# Revit family: Hager-VOLTA-Flush_mounted-IP30-With_Cover-With_DIN-Hosted-PL-en
name_source: partatom
category: Electrical Equipment
units: mm (PartAtom-declared; Revit-internal decimal feet)

## family parameters
Cut with Voids When Loaded = No
Host = Face
Maintain Annotation Orientation = Yes
Panel Configuration = Two Columns, Circuits Across
Part Type = Panelboard
Room Calculation Point = No
Round Connector Dimension = Use Diameter
Shared = No

## types (18) — shared parameters
BC_MODEL_ID = 1547210
BC_OBJECT_ID = 513496
BC_OBJECT_VERSION = #5
Code hager = ADD-EC000214_EU
EF000003 - Mounting method = Flush-mounted
EF000007 - Colour = White
EF000008 - Width = 348 mm  [stored 1.14173 ft]
EF000024 - UV resistant = No
EF000049 - Depth = 98 mm  [stored 0.321522 ft]
EF000116 - RAL-number = 9010
EF001062 - EMC-version = No
EF001088 - Extension possible = Yes
EF001134 - DIN-rail = Yes
EF002950 - Width in number of modular spacings = 12
EF004462 - Type of closure = Other
EF005474 - Degree of protection (IP) = IP30
EF006244 - Transparent cover/door = No
EF006306 - With lock = No
EF009212 - Cover model = With notch
EF015941 - Signal passing door = No
ETIM class code = EC000214
ETIM class name = Small distribution board
HG000002-With door or cover = Yes
HG000003-Range = VOLTA
HG000005-Thickness = 2 mm  [stored 0.00656168 ft]
HG000006-Flush mounted = Yes
HG000009-Double swing door = No
HG000010-Asymmetric doors = No
HG000012-Door swing angle = 90.00°
HG000013-Door on the left = No
HG000014-Door on the right = Yes
HG000015-Clearance visibility = Yes
HG000016-Door 3D visibility = Yes
HG000017-Distance between poles = 18 mm  [stored 0.0590551 ft]
HG000060-RAL-number = 9010
HG000099-Onfly Template ID = 507532
HGEF002950-Width in number of modular spacings = 12
Manufacturer = Hager
Name = VOLTA-Flush_mounted-IP30-With_Cover-With_DIN-PL
Name BIM&CO = Electricity
Name hager = ADD_Enclosures_EC000214
Uniformat = Low Tension Service & Dist.
Uniformat code = D501001
zero-valued in all types: Default Elevation, EF001131 - Inner depth, HG000007-Number of empty columns

## per-type parameters (varying)
| type | BC_VARIANT_ID | EF000040 - Height | EF000118 - With mounting plate | EF000218 - Built-in depth | EF000266 - Number of rows | EF000332 - Built-in height | EF000846 - Built-in width | EF015776 - Earthing terminal block | EF015777 - Neutral terminal block | HG000001-Number of columns | HG000004-Manufacturer reference | HG000008-Number of empty rows | HG000011-Empty rows from bottom | HGEF000266-Number of rows |
| VOLTA-Flush_mounted_W348_H356_D98_12_Modular_Spacing-VU12AT | 1174376 | 356 mm  [stored 1.16798 ft] | No | 89 mm  [stored 0.291995 ft] | 1 | 321 mm  [stored 1.05315 ft] | 315 mm | Yes | Yes | 1 | VU12AT | 0 | No | 1 |
| VOLTA-Flush_mounted_W348_H356_D98_12_Modular_Spacing-VU12NE | 1174377 | 356 mm  [stored 1.16798 ft] | No | 89 mm  [stored 0.291995 ft] | 1 | 321 mm  [stored 1.05315 ft] | 315 mm | Yes | No | 1 | VU12NE | 0 | No | 1 |
| VOLTA-Flush_mounted_W348_H505_D98_12_Modular_Spacing-VU24AT | 1174378 | 505 mm  [stored 1.65682 ft] | No | 89 mm  [stored 0.291995 ft] | 2 | 470 mm  [stored 1.54199 ft] | 315 mm | Yes | Yes | 1 | VU24AT | 0 | No | 2 |
| VOLTA-Flush_mounted_W348_H505_D98_12_Modular_Spacing-VU24NE | 1174380 | 505 mm  [stored 1.65682 ft] | No | 89 mm  [stored 0.291995 ft] | 2 | 470 mm  [stored 1.54199 ft] | 315 mm | Yes | No | 1 | VU24NE | 0 | No | 2 |
| VOLTA-Flush_mounted_W348_H505_D98_12_Modular_Spacing-VU24NWB | 1174383 | 505 mm  [stored 1.65682 ft] | Yes | 89 mm  [stored 0.291995 ft] | 0 | 470 mm  [stored 1.54199 ft] | 315 mm | No | No | 0 | VU24NWB | 0 | No | 0 |
| VOLTA-Flush_mounted_W348_H630_D98_12_Modular_Spacing-VU36AT | 1174385 | 630 mm  [stored 2.06693 ft] | No | 89 mm  [stored 0.291995 ft] | 3 | 595 mm  [stored 1.9521 ft] | 315 mm | Yes | Yes | 1 | VU36AT | 0 | No | 3 |
| VOLTA-Flush_mounted_W348_H630_D98_12_Modular_Spacing-VU36NE | 1174386 | 630 mm  [stored 2.06693 ft] | No | 89 mm  [stored 0.291995 ft] | 3 | 595 mm  [stored 1.9521 ft] | 315 mm | Yes | No | 1 | VU36NE | 0 | No | 3 |
| VOLTA-Flush_mounted_W348_H630_D98_12_Modular_Spacing-VU36NWB | 1174387 | 630 mm  [stored 2.06693 ft] | Yes | 89 mm  [stored 0.291995 ft] | 0 | 595 mm  [stored 1.9521 ft] | 315 mm | No | No | 0 | VU36NWB | 0 | No | 0 |
| VOLTA-Flush_mounted_W348_H755_D98_12_Modular_Spacing-VU48AT | 1174388 | 755 mm  [stored 2.47703 ft] | No | 89 mm  [stored 0.291995 ft] | 4 | 720 mm  [stored 2.3622 ft] | 315 mm | Yes | Yes | 1 | VU48AT | 0 | No | 4 |
| VOLTA-Flush_mounted_W348_H755_D98_12_Modular_Spacing-VU48NE | 1174389 | 755 mm  [stored 2.47703 ft] | No | 89 mm  [stored 0.291995 ft] | 4 | 720 mm  [stored 2.3622 ft] | 315 mm | Yes | No | 1 | VU48NE | 0 | No | 4 |
| VOLTA-Flush_mounted_W348_H755_D98_12_Modular_Spacing-VU48NWB | 1174390 | 755 mm  [stored 2.47703 ft] | Yes | 89 mm  [stored 0.291995 ft] | 0 | 720 mm  [stored 2.3622 ft] | 315 mm | No | No | 0 | VU48NWB | 0 | No | 0 |
| VOLTA-Flush_mounted_W348_H880_D98_12_Modular_Spacing-VU601PLH | 1174391 | 880 mm  [stored 2.88714 ft] | Yes | 89 mm  [stored 0.291995 ft] | 5 | 845 mm  [stored 2.77231 ft] | 315 mm | Yes | Yes | 1 | VU601PLH | 4 | Yes | 5 |
| VOLTA-Flush_mounted_W348_H880_D98_12_Modular_Spacing-VU602PLH | 1174392 | 880 mm  [stored 2.88714 ft] | Yes | 89 mm  [stored 0.291995 ft] | 5 | 845 mm  [stored 2.77231 ft] | 315 mm | Yes | Yes | 1 | VU602PLH | 3 | Yes | 5 |
| VOLTA-Flush_mounted_W348_H880_D98_12_Modular_Spacing-VU603PLG | 1174393 | 880 mm  [stored 2.88714 ft] | Yes | 89 mm  [stored 0.291995 ft] | 5 | 845 mm  [stored 2.77231 ft] | 315 mm | Yes | Yes | 1 | VU603PLG | 2 | Yes | 5 |
| VOLTA-Flush_mounted_W348_H880_D98_12_Modular_Spacing-VU603PLH | 1174394 | 880 mm  [stored 2.88714 ft] | Yes | 89 mm  [stored 0.291995 ft] | 5 | 845 mm  [stored 2.77231 ft] | 315 mm | Yes | Yes | 1 | VU603PLH | 2 | Yes | 5 |
| VOLTA-Flush_mounted_W348_H880_D98_12_Modular_Spacing-VU60NC | 1174395 | 880 mm  [stored 2.88714 ft] | No | 89 mm  [stored 0.291995 ft] | 5 | 846 mm  [stored 2.77559 ft] | 315 mm | Yes | No | 1 | VU60NC | 0 | No | 5 |
| VOLTA-Flush_mounted_W348_H880_D98_12_Modular_Spacing-VU60NE | 1174396 | 880 mm  [stored 2.88714 ft] | No | 90 mm  [stored 0.295276 ft] | 5 | 845 mm  [stored 2.77231 ft] | 314 mm  [stored 1.03018 ft] | Yes | Yes | 1 | VU60NE | 0 | No | 5 |
| VOLTA-Flush_mounted_W348_H880_D98_12_Modular_Spacing-VU60NWB | 1174397 | 880 mm  [stored 2.88714 ft] | Yes | 89 mm  [stored 0.291995 ft] | 0 | 865 mm  [stored 2.83793 ft] | 315 mm | No | No | 0 | VU60NWB | 0 | No | 0 |

note: column(s) folded — value = type name in every type: Reference

note: [stored X ft] marks values corroborated as IEEE doubles in the binary element streams (Revit-internal decimal feet)

## geometry (parser evidence)
native form markers: Sweep x13
no freeform markers — native parametric forms only
